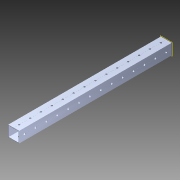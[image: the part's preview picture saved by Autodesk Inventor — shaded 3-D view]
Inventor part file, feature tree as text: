
AUTODESK INVENTOR PART (.ipt)
format: ipt  version: 2014 (Build 180170000, 170)  size: 1,260,032 bytes
history: native  units: in
note: dims shown in document units (in); Inventor stores cm internally (conversion verified against a paired STEP export)
features: extrude x3, sketch x3, pattern_circular x1, other x1, plane x1, imported_body x1
ambient origin geometry x8: Origin, YZ Plane, XZ Plane, XY Plane, X Axis, Y Axis, Z Axis, Center Point
bodies: Body1 (feature_tree)
feature tree (10):
  pattern_circular  "CirPattern2"
  other  "217-3426-STEP1"
  plane  "Work Plane1"
  extrude  "Extrusion1"  Depth=3937.0079in TaperAngle=0.0deg
  extrude  "Extrusion2"  Depth=1.0in TaperAngle=0.0deg
  extrude  "Extrusion3"  [1 undecoded]
  imported_body  "Base1"
  sketch  "Sketch1"  dims[d0=-21.0in d1=3937.0079in d2=0.0in]
  sketch  "Sketch3"  dims[d3=1.0in d4=0.0in d5=6.0in d6=0.0in]
  sketch  "Sketch4"
note: 1 required parameter value undecoded (feature->parameter linkage not recoverable at this tier; creation-order binding heuristic only, values carry confidence <= 0.55)
